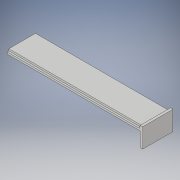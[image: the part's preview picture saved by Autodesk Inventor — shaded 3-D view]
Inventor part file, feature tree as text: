
AUTODESK INVENTOR PART (.ipt)
format: ipt  version: 2019 (Build 230136000, 136)  size: 131,072 bytes
history: native  units: mm
features: extrude x3, sketch x3, mirror x1
ambient origin geometry x8: Origin, YZ Plane, XZ Plane, XY Plane, X Axis, Y Axis, Z Axis, Center Point
bodies: Solid1 (feature_tree)
feature tree (7):
  extrude  "Extrusion1"  Depth=22.0mm
  extrude  "Extrusion2"  Depth=1.5mm
  mirror  "Mirror1"
  extrude  "Extrusion4"  Depth=2.75mm
  sketch  "Sketch2"  dims[d2=112.0mm d3=22.0mm]
  sketch  "Sketch4"  dims[d4=3.0mm d5=0.0mm d6=1.5mm]
  sketch  "Sketch6"  dims[d7=1.5mm d8=0.0mm d12=2.75mm d13=2.0mm d14=12.0mm d15=0.0mm d16=4.0mm d17=0.0mm]
